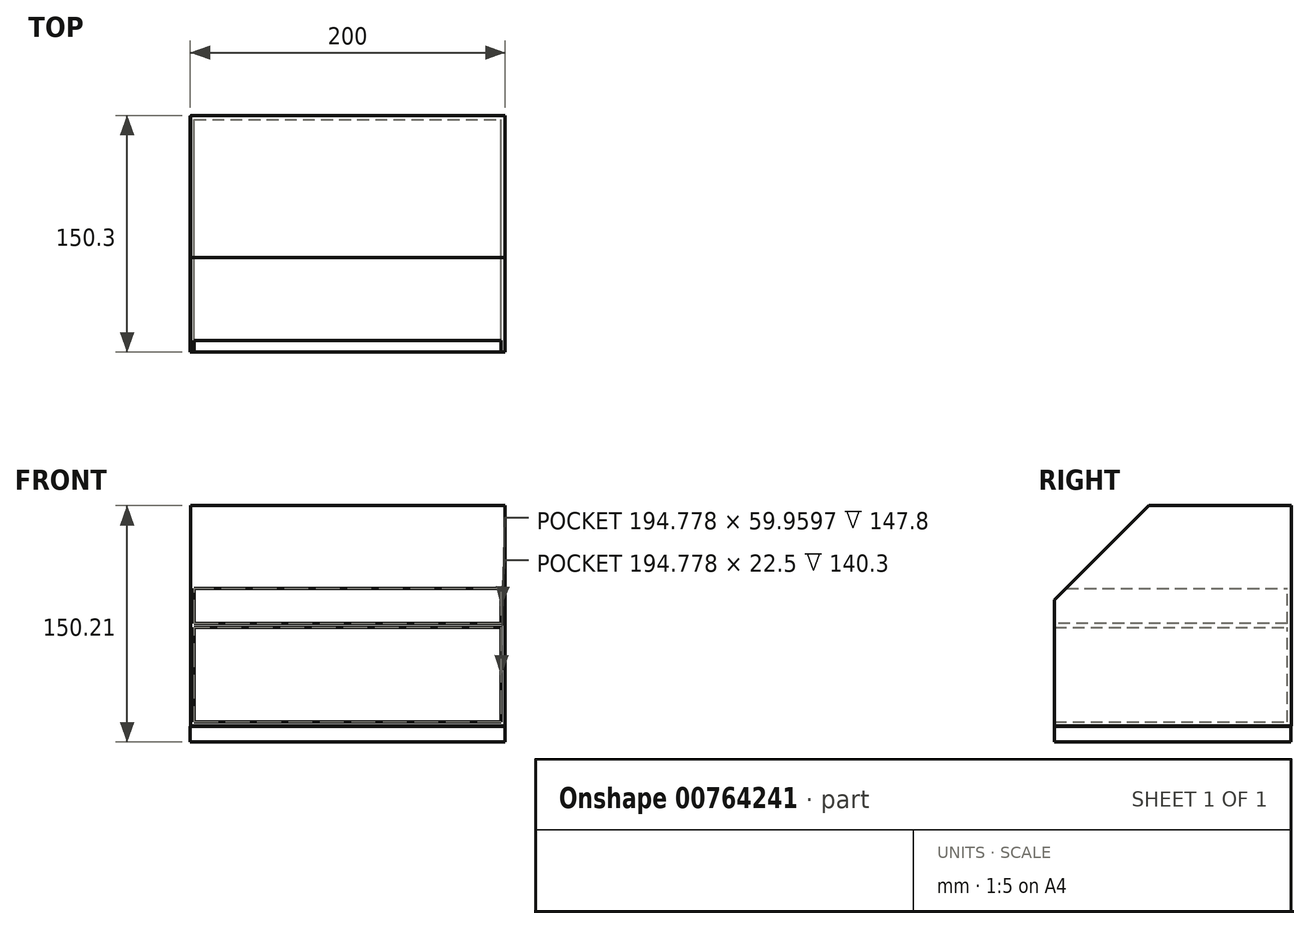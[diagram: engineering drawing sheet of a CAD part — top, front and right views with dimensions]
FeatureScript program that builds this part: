
annotation { "Feature Type Name" : "Feature", "Feature Type Description" : "" }
export const myFeature = defineFeature(function(context is Context, id is Id, definition is map)
    precondition{}
    {
        {
            var Q0;
            Q0=qCreatedBy(makeId("Top.planeOp"),FACE);
            var sketch = newSketch(context, id + "F0", { "sketchPlane" : qUnion([Q0])});
            skLineSegment(sketch, "E0.bottom", {"start": v(-100, 75) * mm, "end": v(100, 75) * mm});
            skLineSegment(sketch, "E0.top", {"start": v(-100, -75) * mm, "end": v(100, -75) * mm});
            skLineSegment(sketch, "E0.left", {"start": v(-100, 75) * mm, "end": v(-100, -75) * mm});
            skLineSegment(sketch, "E0.right", {"start": v(100, 75) * mm, "end": v(100, -75) * mm});
            skPoint(sketch, "E0.middle", {"position": v(0, 0) * mm});
            skSolve(sketch);
        }
        {
            var Q0;
            Q0=makeQuery(id+"F0.imprint","IMPRINT",FACE,{"disambiguationData":[TD([[makeQuery(id+"F0.imprint","IMPRINT",EDGE,{"derivedFrom":sQuery(id+"F0.wireOp",EDGE,"E0.bottom")}),-1.0]])]});
            extrude(context, id + "F1", {"entities" : qUnion([Q0]), "depth" : 10 * mm, "offsetDistance" : 25 * mm});
        }
        {
            var Q0;
            Q0=qCreatedBy(makeId("Front.planeOp"),FACE);
            var sketch = newSketch(context, id + "F2", { "sketchPlane" : qUnion([Q0])});
            skLineSegment(sketch, "E1.bottom", {"start": v(-99.89, 10.25) * mm, "end": v(99.89, 10.25) * mm});
            skLineSegment(sketch, "E1.top", {"start": v(-99.89, 75.21) * mm, "end": v(99.89, 75.21) * mm});
            skLineSegment(sketch, "E1.left", {"start": v(-99.89, 10.25) * mm, "end": v(-99.89, 75.21) * mm});
            skLineSegment(sketch, "E1.right", {"start": v(99.89, 10.25) * mm, "end": v(99.89, 75.21) * mm});
            skSolve(sketch);
        }
        {
            var Q0;
            Q0=makeQuery(id+"F2.imprint","IMPRINT",FACE,{"disambiguationData":[TD([[makeQuery(id+"F2.imprint","IMPRINT",EDGE,{"derivedFrom":sQuery(id+"F2.wireOp",EDGE,"E1.bottom")}),1.0]])]});
            extrude(context, id + "F3", {"entities" : qUnion([Q0]), "depth" : 75 * mm, "offsetDistance" : 25 * mm});
        }
        {
            var Q0;
            Q0=makeQuery(id+"F3.opExtrude","CAP_FACE",FACE,{"disambiguationData":[OSD([sQuery(id+"F2.wireOp",EDGE,"E1.bottom"),sQuery(id+"F2.wireOp",EDGE,"E1.top"),sQuery(id+"F2.wireOp",EDGE,"E1.left"),sQuery(id+"F2.wireOp",EDGE,"E1.right")])],"isStart":true});
            extrude(context, id + "F4", {"entities" : qUnion([Q0]), "operationType" : NewBodyOperationType.ADD, "depth" : 75.3 * mm, "offsetDistance" : 25 * mm});
        }
        {
            var Q0;
            Q0=makeQuery(id+"F3.opExtrude","CAP_FACE",FACE,{"disambiguationData":[OSD([sQuery(id+"F2.wireOp",EDGE,"E1.bottom"),sQuery(id+"F2.wireOp",EDGE,"E1.top"),sQuery(id+"F2.wireOp",EDGE,"E1.left"),sQuery(id+"F2.wireOp",EDGE,"E1.right")])],"isStart":false});
            shell(context, id + "F5", {"entities" : qUnion([Q0]), "thickness" : 2.5 * mm});
        }
        {
            var Q0;
            {var subQ0=sQuery(id+"F2.wireOp",EDGE,"E1.top");Q0=makeQuery(id+"F4.boolean.opBoolean","MERGE",FACE,{"derivedFrom":[makeQuery(id+"F3.opExtrude","SWEPT_FACE",FACE,{"disambiguationData":[OSD([subQ0])]}),makeQuery(id+"F4.opExtrude","SWEPT_FACE",FACE,{"disambiguationData":[OSD([subQ0])]})]});}
            extrude(context, id + "F6", {"entities" : qUnion([Q0]), "operationType" : NewBodyOperationType.ADD, "depth" : 25 * mm, "offsetDistance" : 25 * mm});
        }
        {
            var Q0;
            {var subQ0=sQuery(id+"F2.wireOp",EDGE,"E1.top");Q0=makeQuery(id+"F6.boolean.opBoolean","MERGE",FACE,{"derivedFrom":[makeQuery(id+"F3.opExtrude","CAP_FACE",FACE,{"disambiguationData":[OSD([sQuery(id+"F2.wireOp",EDGE,"E1.bottom"),subQ0,sQuery(id+"F2.wireOp",EDGE,"E1.left"),sQuery(id+"F2.wireOp",EDGE,"E1.right")])],"isStart":false}),makeQuery(id+"F6.opExtrude","SWEPT_FACE",FACE,{"disambiguationData":[OSD([subQ0]),TDD([makeQuery(id+"F3.opExtrude","CAP_EDGE",EDGE,{"disambiguationData":[OSD([subQ0])],"isStart":false})])]})]});}
            shell(context, id + "F7", {"entities" : qUnion([Q0]), "thickness" : 2.5 * mm});
        }
        {
            var Q0;
            Q0=makeQuery(id+"F6.opExtrude","CAP_FACE",FACE,{"disambiguationData":[OSD([sQuery(id+"F2.wireOp",EDGE,"E1.top")])],"isStart":false});
            var sketch = newSketch(context, id + "F8", { "sketchPlane" : qUnion([Q0])});
            skLineSegment(sketch, "E2.bottom", {"start": v(-99.89, 75.3) * mm, "end": v(99.89, 75.3) * mm});
            skLineSegment(sketch, "E2.top", {"start": v(-99.89, -75) * mm, "end": v(99.89, -75) * mm});
            skLineSegment(sketch, "E2.left", {"start": v(-99.89, 75.3) * mm, "end": v(-99.89, -75) * mm});
            skLineSegment(sketch, "E2.right", {"start": v(99.89, 75.3) * mm, "end": v(99.89, -75) * mm});
            skSolve(sketch);
        }
        {
            var Q0;
            Q0=makeQuery(id+"F8.imprint","IMPRINT",FACE,{"disambiguationData":[TD([[makeQuery(id+"F8.imprint","IMPRINT",EDGE,{"derivedFrom":sQuery(id+"F8.wireOp",EDGE,"E2.bottom")}),-1.0]])]});
            extrude(context, id + "F9", {"entities" : qUnion([Q0]), "operationType" : NewBodyOperationType.ADD, "depth" : 50 * mm, "offsetDistance" : 25 * mm});
        }
        {
            var Q0;
            Q0=makeQuery(id+"F9.opExtrude","CAP_EDGE",EDGE,{"disambiguationData":[OSD([sQuery(id+"F8.wireOp",EDGE,"E2.top")])],"isStart":false});
            chamfer(context, id + "F10", {"entities" : qUnion([Q0]), "width" : 60 * mm, "tangentPropagation" : true});
        }
        {
            var Q0;
            Q0=makeQuery(id+"F10.opChamfer","BLEND_FACE",FACE,{"disambiguationData":[OSD([sQuery(id+"F8.wireOp",EDGE,"E2.top")])]});
            var sketch = newSketch(context, id + "F11", { "sketchPlane" : qUnion([Q0])});
            skLineSegment(sketch, "E3", {"start": v(-67.36, 70.74) * mm, "end": v(76.54, 70.74) * mm});
            skLineSegment(sketch, "E4", {"start": v(76.54, 70.74) * mm, "end": v(76.54, 43.45) * mm});
            skLineSegment(sketch, "E5", {"start": v(76.54, 43.45) * mm, "end": v(-67.36, 70.74) * mm});
            skSolve(sketch);
        }
        {
            var Q0;
            Q0=makeQuery(id+"F11.imprint","IMPRINT",FACE,{"disambiguationData":[TD([[makeQuery(id+"F11.imprint","IMPRINT",EDGE,{"derivedFrom":sQuery(id+"F11.wireOp",EDGE,"E3")}),-1.0]])]});
            extrude(context, id + "F12", {"entities" : qUnion([Q0]), "operationType" : NewBodyOperationType.ADD, "oppositeDirection" : true, "depth" : 9.4 * mm, "offsetDistance" : 25 * mm});
        }
        {
            var Q0;
            Q0=makeQuery(id+"F10.opChamfer","BLEND_FACE",FACE,{"disambiguationData":[OSD([sQuery(id+"F8.wireOp",EDGE,"E2.top")])]});
            var sketch = newSketch(context, id + "F13", { "sketchPlane" : qUnion([Q0])});
            skLineSegment(sketch, "E6", {"start": v(-91.6, 87.88) * mm, "end": v(93.35, 87.88) * mm});
            skLineSegment(sketch, "E7", {"start": v(93.35, 87.88) * mm, "end": v(93.35, 30.33) * mm});
            skLineSegment(sketch, "E8", {"start": v(93.35, 30.33) * mm, "end": v(-91.67, 30.33) * mm});
            skLineSegment(sketch, "E9", {"start": v(-91.67, 30.33) * mm, "end": v(-91.6, 87.88) * mm});
            skSolve(sketch);
        }
        {
            var Q0;
            Q0=sQuery(id+"F13.wireOp",EDGE,"E6");
            var Q1;
            Q1=sQuery(id+"F13.wireOp",EDGE,"E9");
            var Q2;
            Q2=sQuery(id+"F13.wireOp",EDGE,"E8");
            var Q3;
            Q3=sQuery(id+"F13.wireOp",EDGE,"E7");
            extrude(context, id + "F14", {"bodyType" : ToolBodyType.SURFACE, "surfaceEntities" : qUnion([Q0, Q1, Q2, Q3]), "depth" : 15.8 * mm, "offsetDistance" : 25 * mm});
        }
    });
